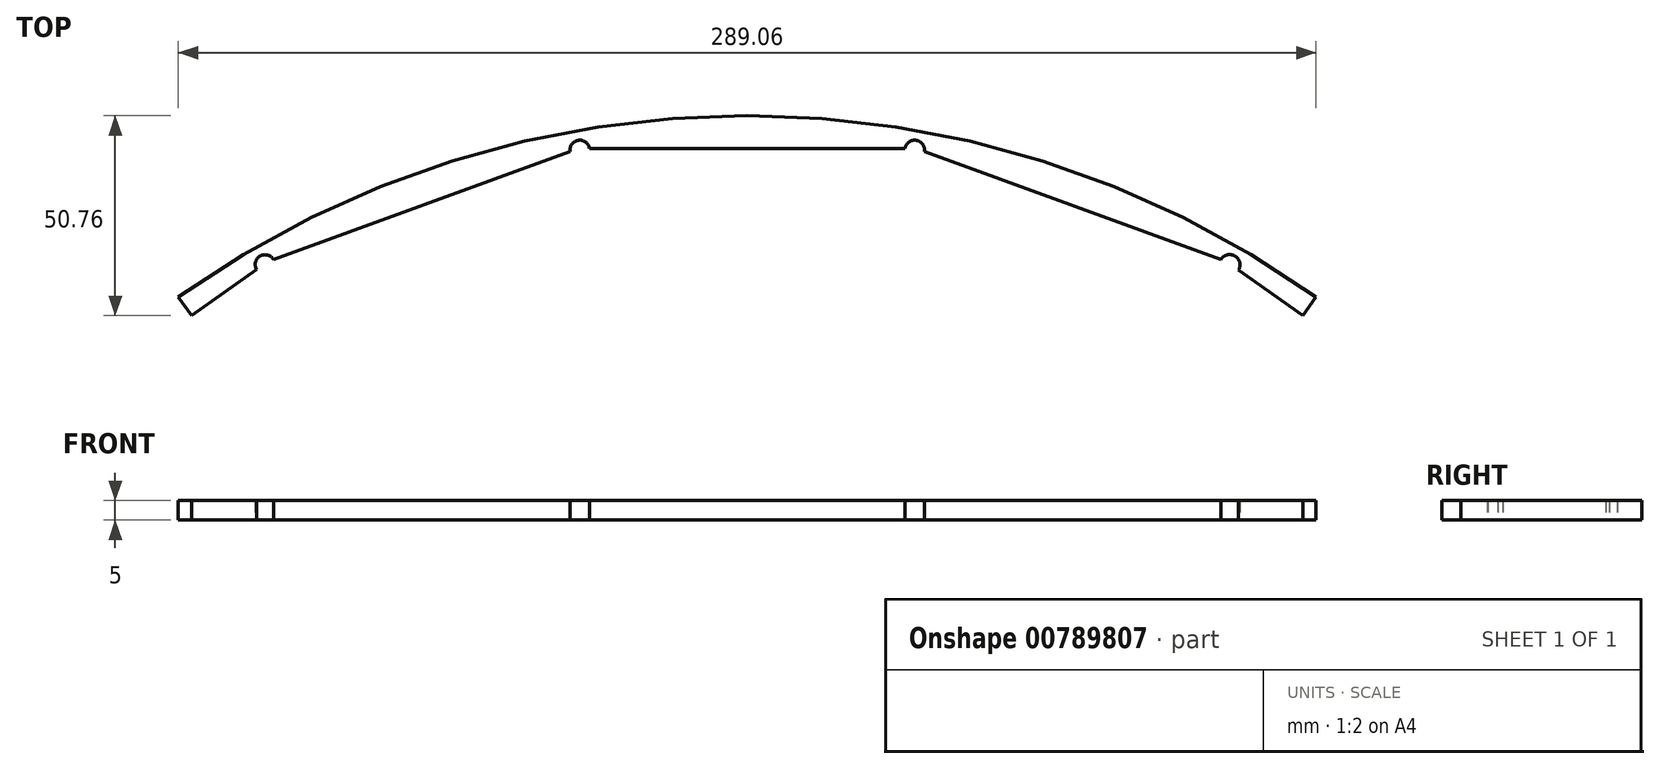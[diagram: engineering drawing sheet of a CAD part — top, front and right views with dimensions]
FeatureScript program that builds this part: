
annotation { "Feature Type Name" : "Feature", "Feature Type Description" : "" }
export const myFeature = defineFeature(function(context is Context, id is Id, definition is map)
    precondition{}
    {
        {
            var Q0;
            Q0=qCreatedBy(makeId("Top.planeOp"),FACE);
            var sketch = newSketch(context, id + "F0", { "sketchPlane" : qUnion([Q0])});
            skLineSegment(sketch, "E0", {"start": v(0, 0) * mm, "end": v(-160.7, 191.51) * mm});
            skLineSegment(sketch, "E1", {"start": v(0, 0) * mm, "end": v(160.7, 191.51) * mm});
            skArc(sketch, "E2", {"start": v(160.7, 191.51) * mm, "mid": v(0, 250) * mm, "end": v(-160.7, 191.51) * mm});
            skLineSegment(sketch, "E3", {"start": v(-124.67, 210.93) * mm, "end": v(-157.48, 187.68) * mm});
            skLineSegment(sketch, "E4", {"start": v(-120.33, 213.43) * mm, "end": v(-45, 240.84) * mm});
            skLineSegment(sketch, "E5", {"start": v(-40.08, 241.71) * mm, "end": v(40.08, 241.71) * mm});
            skLineSegment(sketch, "E6", {"start": v(45, 240.84) * mm, "end": v(120.33, 213.43) * mm});
            skLineSegment(sketch, "E7", {"start": v(124.84, 210.8) * mm, "end": v(157.48, 187.68) * mm});
            skArc(sketch, "E8", {"start": v(-120.33, 213.43) * mm, "mid": v(-123.75, 214.34) * mm, "end": v(-124.67, 210.93) * mm});
            skArc(sketch, "E9", {"start": v(-40.08, 241.71) * mm, "mid": v(-42.98, 243.74) * mm, "end": v(-45, 240.84) * mm});
            skArc(sketch, "E10", {"start": v(45, 240.84) * mm, "mid": v(42.98, 243.74) * mm, "end": v(40.08, 241.71) * mm});
            skArc(sketch, "E11", {"start": v(124.84, 210.8) * mm, "mid": v(123.9, 214.37) * mm, "end": v(120.33, 213.43) * mm});
            skLineSegment(sketch, "E12", {"start": v(-157.48, 187.68) * mm, "end": v(-160.7, 191.51) * mm});
            skLineSegment(sketch, "E13", {"start": v(157.48, 187.68) * mm, "end": v(160.7, 191.51) * mm});
            skLineSegment(sketch, "E14", {"start": v(-141.16, 199.24) * mm, "end": v(-144.53, 204) * mm});
            skLineSegment(sketch, "E15", {"start": v(141.16, 199.24) * mm, "end": v(144.53, 204) * mm});
            skSolve(sketch);
        }
        {
            var Q0;
            Q0=makeQuery(id+"F0.imprint","IMPRINT",FACE,{"disambiguationData":[TD([[makeQuery(id+"F0.imprint","IMPRINT",EDGE,{"derivedFrom":sQuery(id+"F0.wireOp",EDGE,"E4")}),1.0]])]});
            extrude(context, id + "F1", {"entities" : qUnion([Q0]), "depth" : 5 * mm, "offsetDistance" : 25 * mm});
        }
    });
